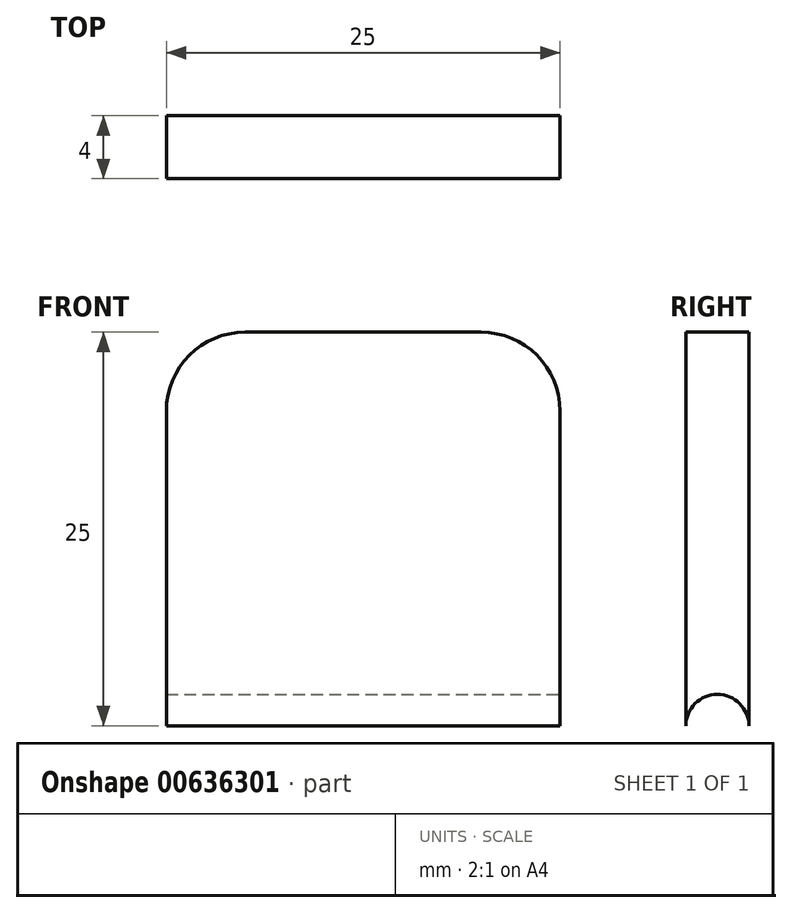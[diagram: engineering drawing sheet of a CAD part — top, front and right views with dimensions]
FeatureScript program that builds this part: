
annotation { "Feature Type Name" : "Feature", "Feature Type Description" : "" }
export const myFeature = defineFeature(function(context is Context, id is Id, definition is map)
    precondition{}
    {
        {
            var Q0;
            Q0=qCreatedBy(makeId("Front.planeOp"),FACE);
            var sketch = newSketch(context, id + "F0", { "sketchPlane" : qUnion([Q0])});
            skLineSegment(sketch, "E0.bottom", {"start": v(-12.5, 25) * mm, "end": v(12.5, 25) * mm});
            skLineSegment(sketch, "E0.top", {"start": v(-12.5, 0) * mm, "end": v(12.5, 0) * mm});
            skLineSegment(sketch, "E0.left", {"start": v(-12.5, 25) * mm, "end": v(-12.5, 0) * mm});
            skLineSegment(sketch, "E0.right", {"start": v(12.5, 25) * mm, "end": v(12.5, 0) * mm});
            skSolve(sketch);
        }
        {
            var Q0;
            Q0=makeQuery(id+"F0.imprint","IMPRINT",FACE,{"disambiguationData":[TD([[makeQuery(id+"F0.imprint","IMPRINT",EDGE,{"derivedFrom":sQuery(id+"F0.wireOp",EDGE,"E0.bottom")}),-1.0]])]});
            extrude(context, id + "F1", {"entities" : qUnion([Q0]), "depth" : 4 * mm, "offsetDistance" : 25 * mm});
        }
        {
            var Q0;
            Q0=makeQuery(id+"F1.opExtrude","SWEPT_EDGE",EDGE,{"disambiguationData":[OSD([sQuery(id+"F0.wireOp",EDGE,"E0.bottom"),sQuery(id+"F0.wireOp",EDGE,"E0.left")])]});
            var Q1;
            Q1=makeQuery(id+"F1.opExtrude","SWEPT_EDGE",EDGE,{"disambiguationData":[OSD([sQuery(id+"F0.wireOp",EDGE,"E0.bottom"),sQuery(id+"F0.wireOp",EDGE,"E0.right")])]});
            fillet(context, id + "F2", {"entities" : qUnion([Q0, Q1]), "radius" : 5 * mm, "tangentPropagation" : true, "allowEdgeOverflow" : false});
        }
        {
            var Q0;
            Q0=makeQuery(id+"F1.opExtrude","SWEPT_FACE",FACE,{"disambiguationData":[OSD([sQuery(id+"F0.wireOp",EDGE,"E0.right")])]});
            var sketch = newSketch(context, id + "F3", { "sketchPlane" : qUnion([Q0])});
            skLineSegment(sketch, "E1", {"start": v(-2, 1.43) * mm, "end": v(-2, -1.1) * mm});
            skPoint(sketch, "E2", {"position": v(-2, 0) * mm});
            skSolve(sketch);
        }
        {
            var Q0;
            Q0=sQuery(id+"F3.wireOp",VERTEX,"E2");
            var Q1;
            Q1=makeQuery(id+"F1.opExtrude","SWEPT_BODY",BODY,{"disambiguationData":[OSD([sQuery(id+"F0.wireOp",EDGE,"E0.bottom"),sQuery(id+"F0.wireOp",EDGE,"E0.top"),sQuery(id+"F0.wireOp",EDGE,"E0.left"),sQuery(id+"F0.wireOp",EDGE,"E0.right")])]});
            hole(context, id + "F4", {"style" : HoleStyle.SIMPLE, "endStyle" : HoleEndStyle.THROUGH, "holeDiameter" : 4 * mm, "majorDiameter" : 5 * mm, "isTappedThrough" : true, "tappedDepth" : 12 * mm, "tapClearance" : 3, "locations" : qUnion([Q0]), "scope" : qUnion([Q1])});
        }
    });
